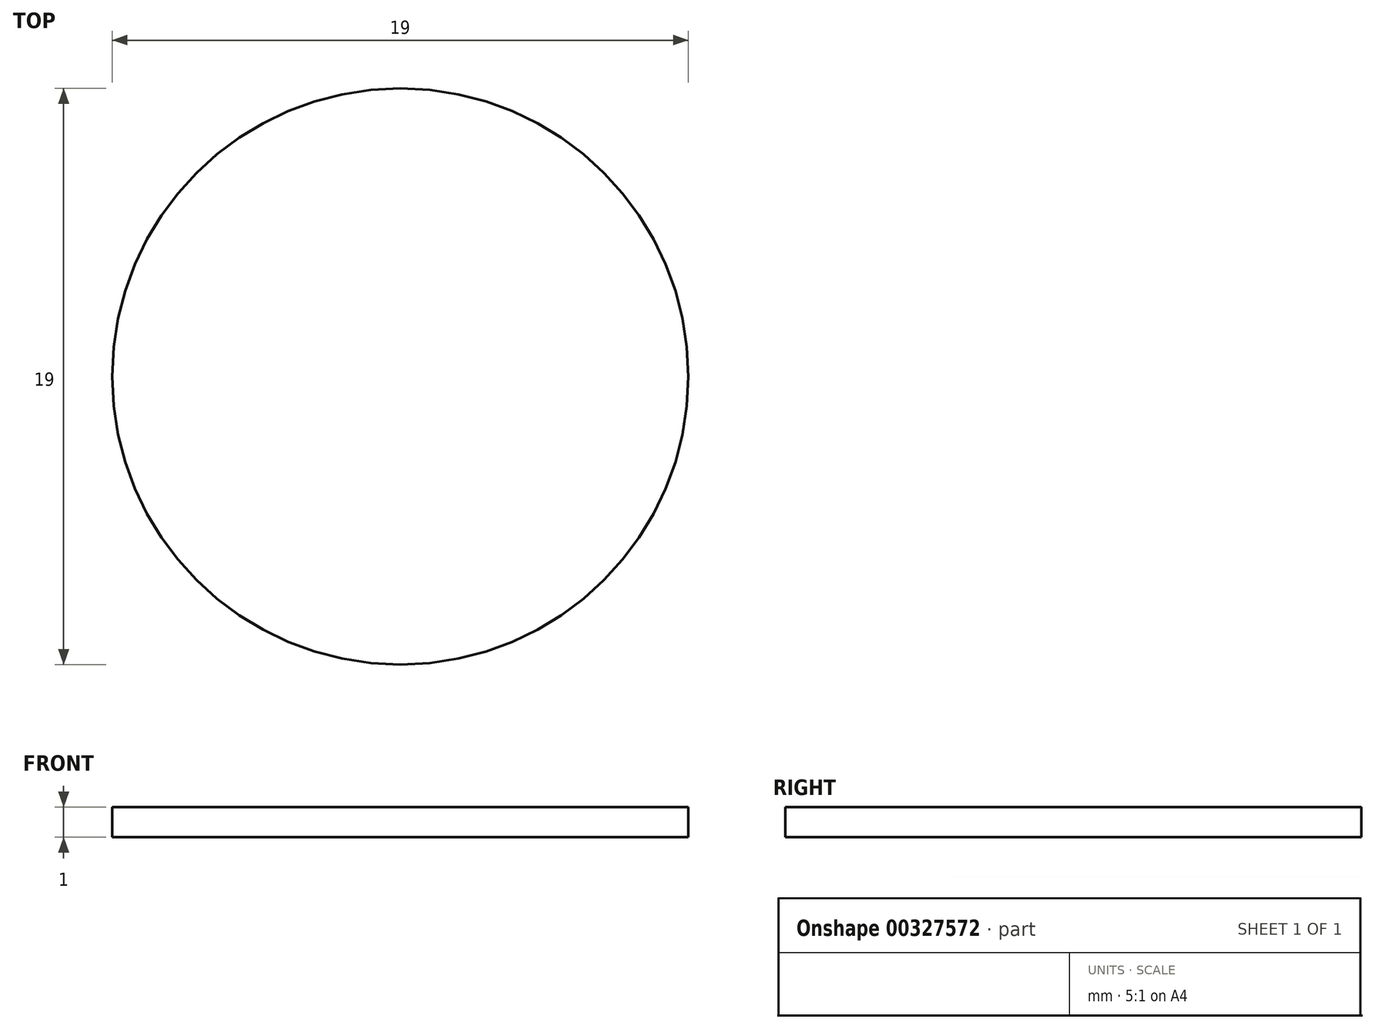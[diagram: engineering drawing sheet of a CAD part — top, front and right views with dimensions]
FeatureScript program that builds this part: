
annotation { "Feature Type Name" : "Feature", "Feature Type Description" : "" }
export const myFeature = defineFeature(function(context is Context, id is Id, definition is map)
    precondition{}
    {
        {
            var Q0;
            Q0=qCreatedBy(makeId("Top.planeOp"),FACE);
            var sketch = newSketch(context, id + "F0", { "sketchPlane" : qUnion([Q0])});
            skCircle(sketch, "E0", {"center": v(0, 0) * mm, "radius": 9.5 * mm});
            skSolve(sketch);
        }
        {
            var Q0;
            Q0=makeQuery(id+"F0.imprint","IMPRINT",FACE,{"disambiguationData":[TD([[makeQuery(id+"F0.imprint","IMPRINT",EDGE,{"derivedFrom":sQuery(id+"F0.wireOp",EDGE,"E0")}),1.0]])]});
            extrude(context, id + "F1", {"entities" : qUnion([Q0]), "depth" : 1 * mm});
        }
    });
